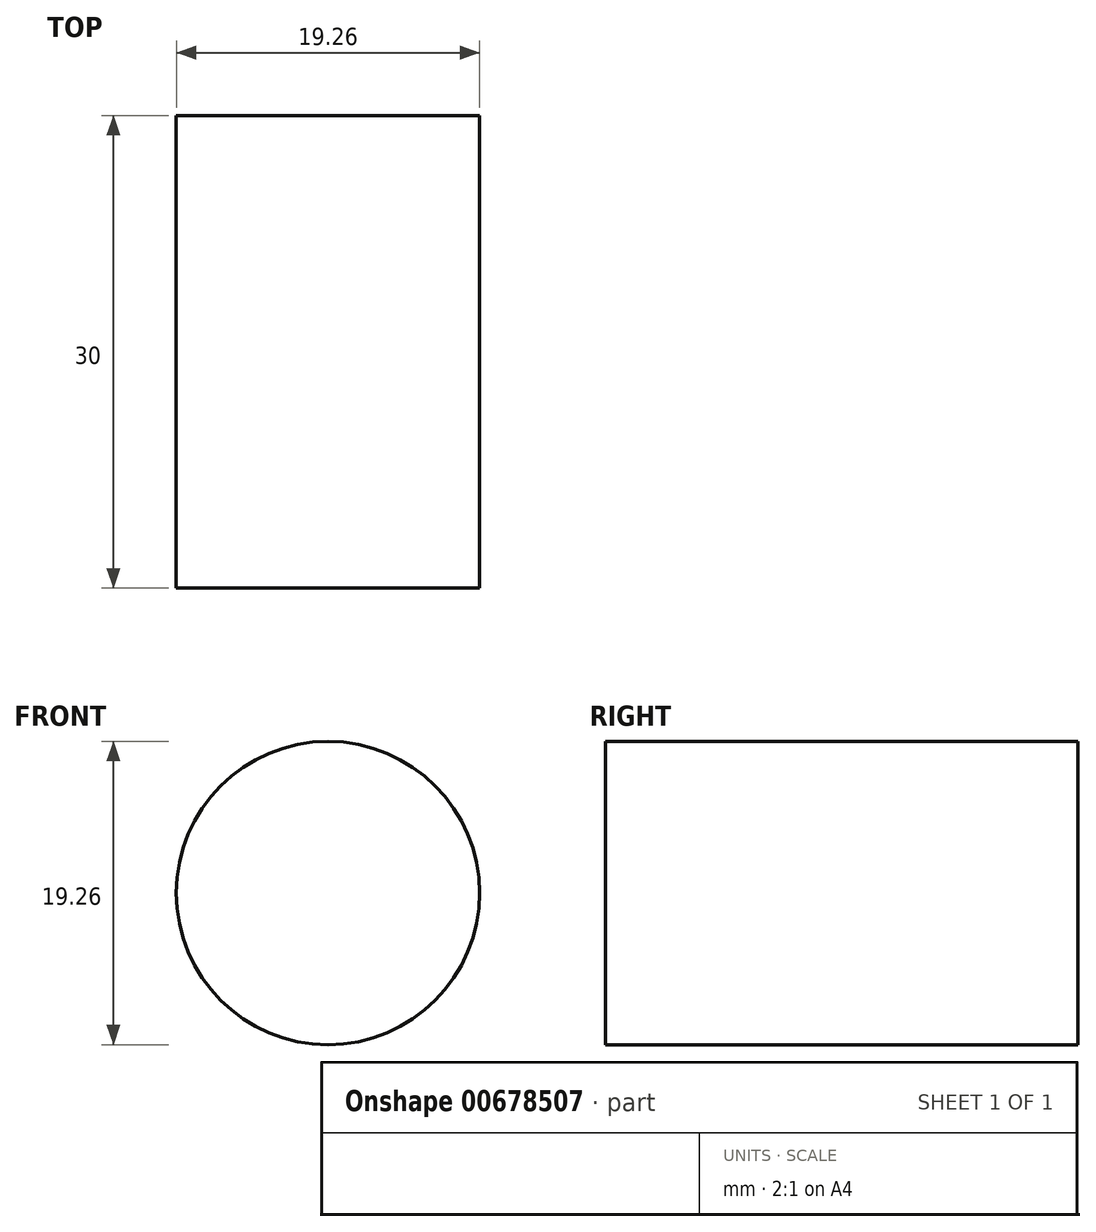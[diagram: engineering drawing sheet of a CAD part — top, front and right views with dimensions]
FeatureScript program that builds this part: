
annotation { "Feature Type Name" : "Feature", "Feature Type Description" : "" }
export const myFeature = defineFeature(function(context is Context, id is Id, definition is map)
    precondition{}
    {
        {
            var Q0;
            Q0=qCreatedBy(makeId("Front.planeOp"),FACE);
            var sketch = newSketch(context, id + "F0", { "sketchPlane" : qUnion([Q0])});
            skCircle(sketch, "E0", {"center": v(0, 0) * mm, "radius": 9.63 * mm});
            skSolve(sketch);
        }
        {
            var Q0;
            Q0 = qSketchRegion(id + "F0", true);
            extrude(context, id + "F1", {"entities" : qUnion([Q0]), "depth" : 30 * mm, "offsetDistance" : 25 * mm});
        }
    });
